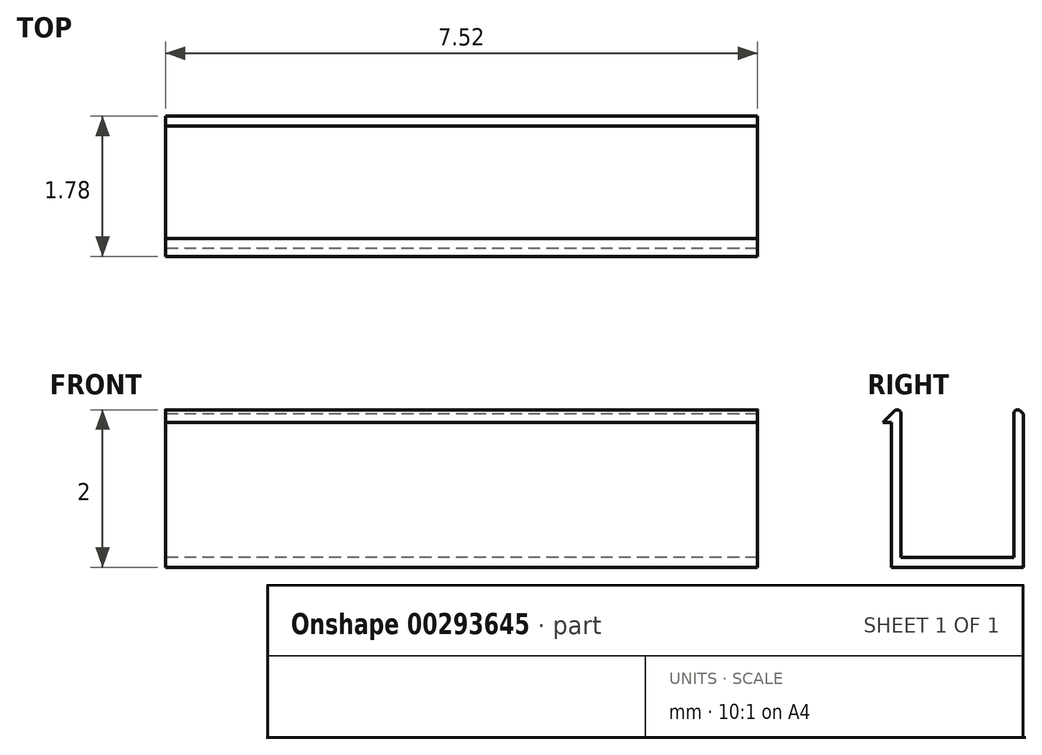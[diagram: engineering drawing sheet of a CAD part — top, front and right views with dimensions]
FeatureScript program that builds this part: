
annotation { "Feature Type Name" : "Feature", "Feature Type Description" : "" }
export const myFeature = defineFeature(function(context is Context, id is Id, definition is map)
    precondition{}
    {
        {
            var Q0;
            Q0=qCreatedBy(makeId("Right.planeOp"),FACE);
            var sketch = newSketch(context, id + "F0", { "sketchPlane" : qUnion([Q0])});
            skLineSegment(sketch, "E0", {"start": v(0, 0) * mm, "end": v(1.68, 0) * mm});
            skLineSegment(sketch, "E1", {"start": v(1.68, 0) * mm, "end": v(1.68, 1.95) * mm});
            skLineSegment(sketch, "E2", {"start": v(1.55, 1.95) * mm, "end": v(1.55, 0.13) * mm});
            skLineSegment(sketch, "E3", {"start": v(1.55, 0.13) * mm, "end": v(0.13, 0.13) * mm});
            skLineSegment(sketch, "E4", {"start": v(0.13, 0.13) * mm, "end": v(0.13, 1.95) * mm});
            skLineSegment(sketch, "E5", {"start": v(0, 1.84) * mm, "end": v(0, 0) * mm});
            skArc(sketch, "E6", {"start": v(0.13, 1.95) * mm, "mid": v(0.1, 2) * mm, "end": v(0.04, 1.99) * mm});
            skLineSegment(sketch, "E7", {"start": v(0.04, 1.99) * mm, "end": v(-0.1, 1.84) * mm});
            skPoint(sketch, "E8.orphan", {"position": v(0, 2) * mm});
            skLineSegment(sketch, "E9", {"start": v(0, 1.84) * mm, "end": v(-0.1, 1.84) * mm});
            skLineSegment(sketch, "E10", {"start": v(0.84, 0.13) * mm, "end": v(0.84, 0) * mm, "construction": true});
            skLineSegment(sketch, "E11.MirrorCS", {"start": v(1.68, 1.84) * mm, "end": v(1.78, 1.84) * mm});
            skLineSegment(sketch, "E12.MirrorCS", {"start": v(1.68, 1.84) * mm, "end": v(1.68, 0) * mm});
            skPoint(sketch, "E13.MirrorP", {"position": v(1.68, 2) * mm});
            skLineSegment(sketch, "E14.MirrorCS", {"start": v(1.64, 1.99) * mm, "end": v(1.78, 1.84) * mm});
            skArc(sketch, "E15.MirrorCS", {"start": v(1.56, 1.95) * mm, "mid": v(1.59, 2) * mm, "end": v(1.64, 1.99) * mm});
            skLineSegment(sketch, "E16.MirrorCS", {"start": v(1.56, 0.12) * mm, "end": v(1.56, 1.95) * mm});
            skSolve(sketch);
        }
        {
            var Q0;
            Q0=makeQuery(id+"F0.imprint","IMPRINT",FACE,{"disambiguationData":[TD([[makeQuery(id+"F0.imprint","IMPRINT",EDGE,{"derivedFrom":sQuery(id+"F0.wireOp",EDGE,"E0")}),1.0]])]});
            extrude(context, id + "F1", {"entities" : qUnion([Q0]), "depth" : 7.52 * mm});
        }
        {
            var Q0;
            Q0=qCreatedBy(makeId("Front.planeOp"),FACE);
            cPlane(context, id + "F2", {"entities" : qUnion([Q0]), "cplaneType" : CPlaneType.OFFSET, "offset" : (1.78 / 2) * mm, "width" : 150 * mm, "height" : 150 * mm});
        }
    });
